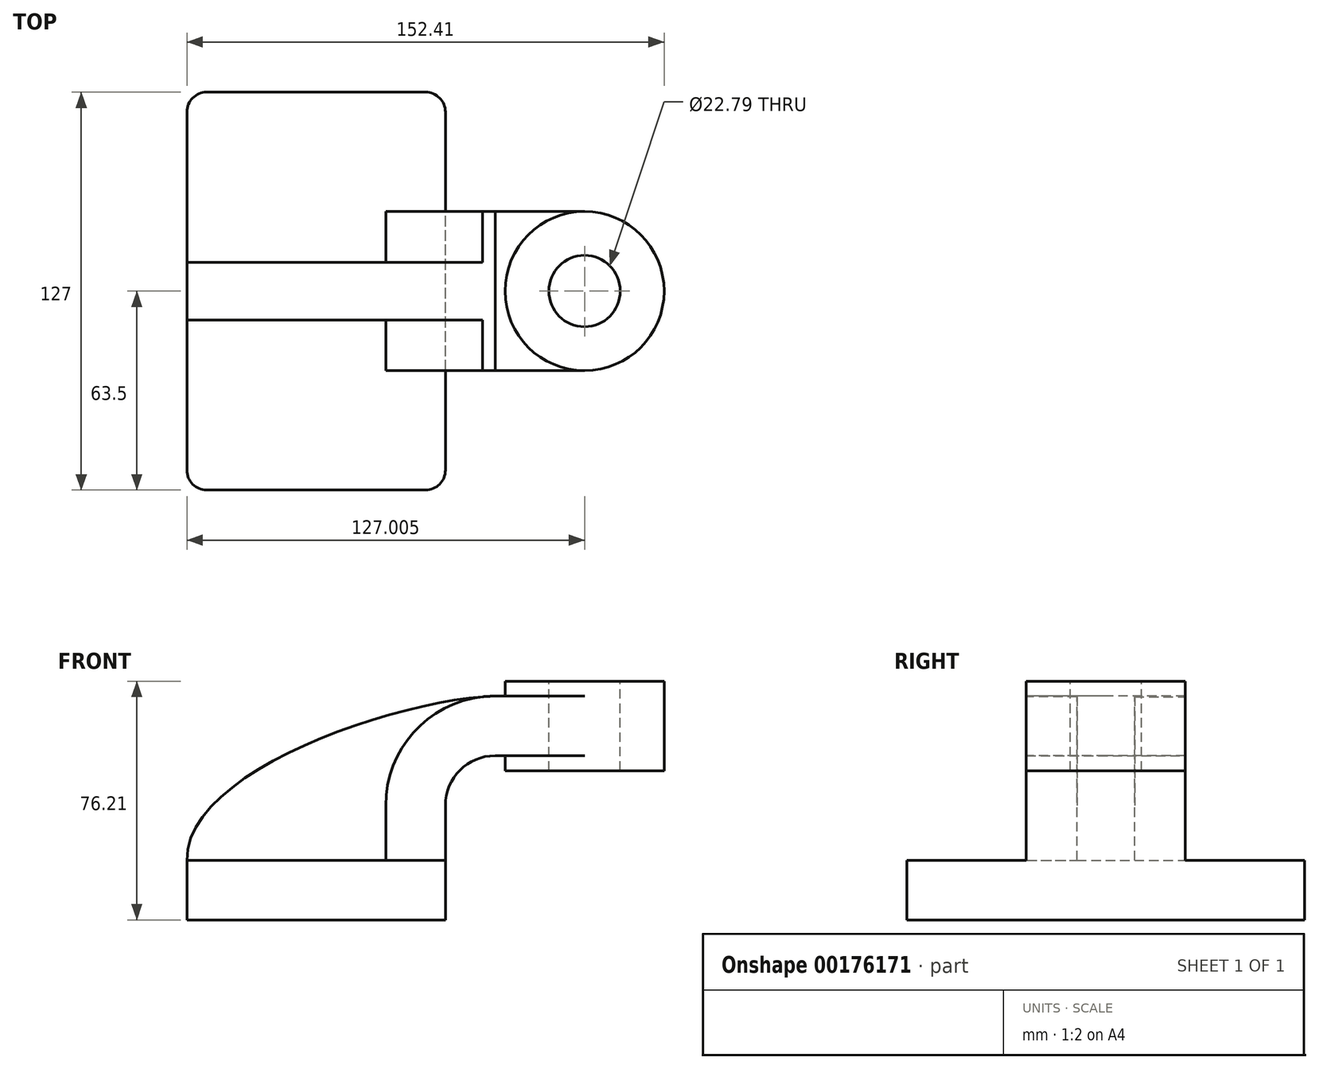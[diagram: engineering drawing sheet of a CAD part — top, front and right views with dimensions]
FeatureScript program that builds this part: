
annotation { "Feature Type Name" : "Feature", "Feature Type Description" : "" }
export const myFeature = defineFeature(function(context is Context, id is Id, definition is map)
    precondition{}
    {
        {
            var Q0;
            Q0=qCreatedBy(makeId("Front.planeOp"),FACE);
            var sketch = newSketch(context, id + "F0", { "sketchPlane" : qUnion([Q0])});
            skLineSegment(sketch, "E0.bottom", {"start": v(-41.27, -9.53) * mm, "end": v(41.28, -9.53) * mm});
            skLineSegment(sketch, "E0.top", {"start": v(-41.28, 9.52) * mm, "end": v(41.28, 9.52) * mm});
            skLineSegment(sketch, "E0.left", {"start": v(-41.28, -9.53) * mm, "end": v(-41.28, 9.53) * mm});
            skLineSegment(sketch, "E0.right", {"start": v(41.28, -9.53) * mm, "end": v(41.28, 9.52) * mm});
            skPoint(sketch, "E0.middle", {"position": v(0, 0) * mm});
            skLineSegment(sketch, "E1.bottom", {"start": v(111.12, 38.1) * mm, "end": v(60.32, 38.1) * mm});
            skLineSegment(sketch, "E1.top", {"start": v(111.12, 66.68) * mm, "end": v(60.32, 66.68) * mm});
            skLineSegment(sketch, "E1.left", {"start": v(111.12, 38.1) * mm, "end": v(111.12, 66.68) * mm});
            skLineSegment(sketch, "E1.right", {"start": v(60.32, 38.1) * mm, "end": v(60.32, 66.67) * mm});
            skPoint(sketch, "E1.middle", {"position": v(85.72, 52.39) * mm});
            skLineSegment(sketch, "E2", {"start": v(41.28, 9.52) * mm, "end": v(41.28, 27) * mm});
            skArc(sketch, "E3", {"start": v(41.27, 27) * mm, "mid": v(45.92, 38.23) * mm, "end": v(57.15, 42.88) * mm});
            skLineSegment(sketch, "E4", {"start": v(57.15, 42.88) * mm, "end": v(85.72, 42.88) * mm});
            skLineSegment(sketch, "E5.0", {"start": v(57.15, 61.93) * mm, "end": v(85.72, 61.93) * mm});
            skArc(sketch, "E5.1", {"start": v(22.22, 27) * mm, "mid": v(32.45, 51.7) * mm, "end": v(57.15, 61.93) * mm});
            skLineSegment(sketch, "E5.2", {"start": v(22.23, 9.52) * mm, "end": v(22.23, 27) * mm});
            skLineSegment(sketch, "E6", {"start": v(85.72, 38.1) * mm, "end": v(85.72, 66.68) * mm});
            skFitSpline(sketch, "E7", {"points": [v(-41.28, 9.53) * mm, v(57.15, 61.93) * mm], "startDerivative": vector(-1.4, 86.28) * mm, "endDerivative": vector(92, 2.82) * mm});
            skSolve(sketch);
        }
        {
            var Q0;
            Q0=makeQuery(id+"F0.imprint","IMPRINT",FACE,{"disambiguationData":[TD([[makeQuery(id+"F0.imprint","IMPRINT",EDGE,{"derivedFrom":sQuery(id+"F0.wireOp",EDGE,"E0.bottom")}),1.0]])]});
            extrude(context, id + "F1", {"entities" : qUnion([Q0]), "endBound" : BoundingType.SYMMETRIC, "depth" : 127 * mm});
        }
        {
            var Q0;
            {var subQ1=sQuery(id+"F0.wireOp",EDGE,"E2");Q0=makeQuery(id+"F0.imprint","IMPRINT",FACE,{"disambiguationData":[TD([[makeQuery(id+"F0.imprint","IMPRINT",EDGE,{"derivedFrom":subQ1}),1.0]])]});}
            var Q1;
            {var subQ0=sQuery(id+"F0.wireOp",EDGE,"E4");var subQ1=sQuery(id+"F0.wireOp",EDGE,"E1.right");var subQ2=makeQuery(id+"F0.imprint","INTERSECT",VERTEX,{"derivedFrom":[subQ1,subQ0]});Q1=makeQuery(id+"F0.imprint","IMPRINT",FACE,{"disambiguationData":[TD([[makeQuery(id+"F0.imprint","IMPRINT",EDGE,{"disambiguationData":[TD([[subQ2,-1.0]])],"derivedFrom":subQ1}),-1.0]])]});}
            extrude(context, id + "F2", {"entities" : qUnion([Q0, Q1]), "operationType" : NewBodyOperationType.ADD, "endBound" : BoundingType.SYMMETRIC, "depth" : 50.8 * mm});
        }
        {
            var Q0;
            {var subQ3=sQuery(id+"F0.wireOp",EDGE,"E5.2");Q0=makeQuery(id+"F0.imprint","IMPRINT",FACE,{"disambiguationData":[TD([[makeQuery(id+"F0.imprint","IMPRINT",EDGE,{"derivedFrom":subQ3}),1.0]])]});}
            extrude(context, id + "F3", {"entities" : qUnion([Q0]), "operationType" : NewBodyOperationType.ADD, "endBound" : BoundingType.SYMMETRIC, "depth" : 18.41 * mm});
        }
        {
            var Q0;
            {var subQ0=sQuery(id+"F0.wireOp",EDGE,"E1.left");Q0=makeQuery(id+"F0.imprint","IMPRINT",FACE,{"disambiguationData":[TD([[makeQuery(id+"F0.imprint","IMPRINT",EDGE,{"derivedFrom":subQ0}),1.0]])]});}
            var Q1;
            Q1=sQuery(id+"F0.wireOp",EDGE,"E6");
            revolve(context, id + "F4", {"operationType" : NewBodyOperationType.ADD, "entities" : qUnion([Q0]), "axis" : qUnion([Q1]), "revolveType" : RevolveType.FULL});
        }
        {
            var Q0;
            Q0=makeQuery(id+"F1.opExtrude","CAP_EDGE",EDGE,{"disambiguationData":[OSD([sQuery(id+"F0.wireOp",EDGE,"E0.right")])],"isStart":false});
            var Q1;
            Q1=makeQuery(id+"F1.opExtrude","CAP_EDGE",EDGE,{"disambiguationData":[OSD([sQuery(id+"F0.wireOp",EDGE,"E0.left")])],"isStart":false});
            var Q2;
            Q2=makeQuery(id+"F1.opExtrude","CAP_EDGE",EDGE,{"disambiguationData":[OSD([sQuery(id+"F0.wireOp",EDGE,"E0.left")])],"isStart":true});
            var Q3;
            Q3=makeQuery(id+"F1.opExtrude","CAP_EDGE",EDGE,{"disambiguationData":[OSD([sQuery(id+"F0.wireOp",EDGE,"E0.right")])],"isStart":true});
            fillet(context, id + "F5", {"entities" : qUnion([Q0, Q1, Q2, Q3]), "radius" : 6.35 * mm, "tangentPropagation" : true, "allowEdgeOverflow" : false});
        }
        {
            var Q0;
            Q0=makeQuery(id+"F4.opRevolve","SWEPT_FACE",FACE,{"disambiguationData":[OSD([sQuery(id+"F0.wireOp",EDGE,"E1.top")])]});
            var sketch = newSketch(context, id + "F6", { "sketchPlane" : qUnion([Q0])});
            skCircle(sketch, "E8", {"center": v(85.72, 0) * mm, "radius": 11.4 * mm});
            skSolve(sketch);
        }
        {
            var Q0;
            Q0 = qSketchRegion(id + "F6", true);
            extrude(context, id + "F7", {"entities" : qUnion([Q0]), "operationType" : NewBodyOperationType.REMOVE, "endBound" : BoundingType.THROUGH_ALL, "oppositeDirection" : true, "depth" : 25.4 * mm});
        }
    });
